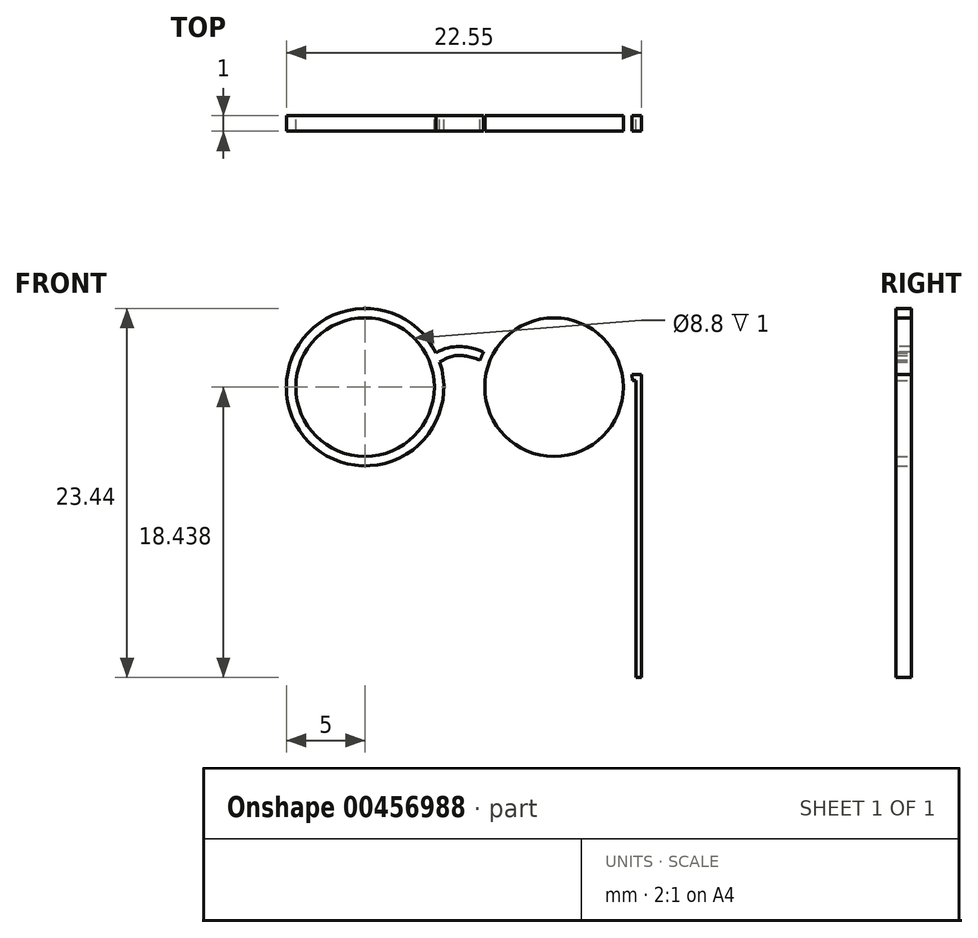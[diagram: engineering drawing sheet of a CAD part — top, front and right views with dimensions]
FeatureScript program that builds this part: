
annotation { "Feature Type Name" : "Feature", "Feature Type Description" : "" }
export const myFeature = defineFeature(function(context is Context, id is Id, definition is map)
    precondition{}
    {
        {
            var Q0;
            Q0=qCreatedBy(makeId("Front.planeOp"),FACE);
            var sketch = newSketch(context, id + "F0", { "sketchPlane" : qUnion([Q0])});
            skCircle(sketch, "E0", {"center": v(-6, 2.93) * mm, "radius": 5 * mm});
            skPoint(sketch, "E0.first.point", {"position": v(-1.95, 0) * mm});
            skPoint(sketch, "E0.second.point", {"position": v(-4.57, 7.72) * mm});
            skPoint(sketch, "E0.third.point", {"position": v(-2.67, -0.8) * mm});
            skCircle(sketch, "E1", {"center": v(-6, 2.93) * mm, "radius": 4.4 * mm});
            skCircle(sketch, "E2.MirrorC", {"center": v(6, 2.93) * mm, "radius": 5 * mm});
            skCircle(sketch, "E3.MirrorC", {"center": v(6, 2.93) * mm, "radius": 4.4 * mm});
            skFitSpline(sketch, "E4", {"points": [v(-1.5, 5.1) * mm, v(1.53, 5.16) * mm, v(1.53, 5.17) * mm], "startDerivative": vector(4.78, 2.82) * mm, "endDerivative": vector(0, 0.18) * mm});
            skFitSpline(sketch, "E5", {"points": [v(-1.26, 4.52) * mm, v(1.3, 4.65) * mm], "startDerivative": vector(2.78, 1.77) * mm, "endDerivative": vector(3.25, -1.11) * mm});
            skLineSegment(sketch, "E6", {"start": v(10.94, 3.73) * mm, "end": v(11.55, 3.73) * mm});
            skLineSegment(sketch, "E7", {"start": v(11.55, 3.73) * mm, "end": v(11.55, -15.51) * mm});
            skLineSegment(sketch, "E8", {"start": v(10.98, 3.36) * mm, "end": v(11.2, 3.36) * mm});
            skLineSegment(sketch, "E9", {"start": v(11.2, 3.36) * mm, "end": v(11.2, -15.51) * mm});
            skLineSegment(sketch, "E10", {"start": v(11.2, -15.51) * mm, "end": v(11.55, -15.51) * mm});
            skSolve(sketch);
        }
        {
            var Q0;
            Q0=makeQuery(id+"F0.imprint","IMPRINT",FACE,{"disambiguationData":[TD([[makeQuery(id+"F0.imprint","IMPRINT",EDGE,{"derivedFrom":sQuery(id+"F0.wireOp",EDGE,"E1")}),-1.0]])]});
            var Q1;
            {var subQ3=sQuery(id+"F0.wireOp",EDGE,"E5");Q1=makeQuery(id+"F0.imprint","IMPRINT",FACE,{"disambiguationData":[TD([[makeQuery(id+"F0.imprint","IMPRINT",EDGE,{"derivedFrom":subQ3}),1.0]])]});}
            var Q2;
            Q2=makeQuery(id+"F0.imprint","IMPRINT",FACE,{"disambiguationData":[TD([[makeQuery(id+"F0.imprint","IMPRINT",EDGE,{"derivedFrom":sQuery(id+"F0.wireOp",EDGE,"E3.MirrorC")}),1.0]])]});
            var Q3;
            {var subQ1=sQuery(id+"F0.wireOp",EDGE,"E6");Q3=makeQuery(id+"F0.imprint","IMPRINT",FACE,{"disambiguationData":[TD([[makeQuery(id+"F0.imprint","IMPRINT",EDGE,{"derivedFrom":subQ1}),-1.0]])]});}
            extrude(context, id + "F1", {"entities" : qUnion([Q0, Q1, Q2, Q3]), "depth" : 1 * mm});
        }
    });
